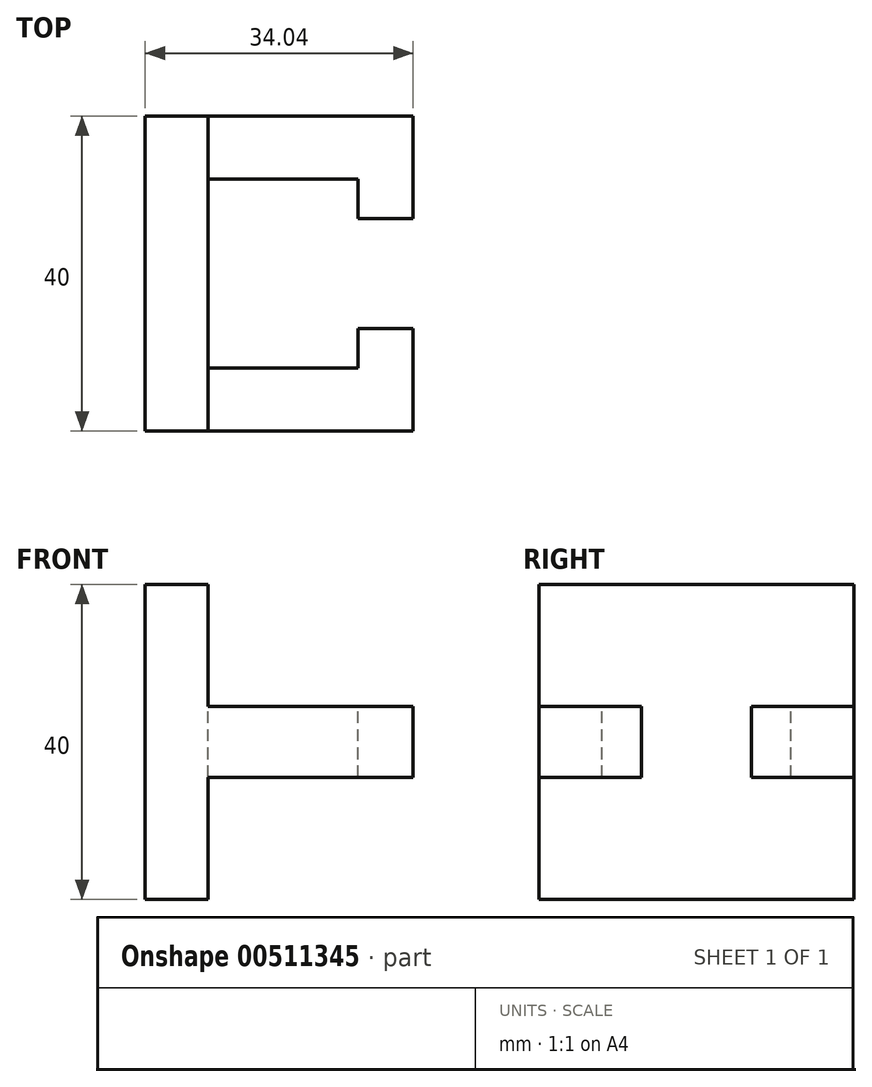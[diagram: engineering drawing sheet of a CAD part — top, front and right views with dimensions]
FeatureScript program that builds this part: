
annotation { "Feature Type Name" : "Feature", "Feature Type Description" : "" }
export const myFeature = defineFeature(function(context is Context, id is Id, definition is map)
    precondition{}
    {
        {
            var Q0;
            Q0=qCreatedBy(makeId("Top.planeOp"),FACE);
            var sketch = newSketch(context, id + "F0", { "sketchPlane" : qUnion([Q0])});
            skLineSegment(sketch, "E0.bottom", {"start": v(-20, 20) * mm, "end": v(20, 20) * mm});
            skLineSegment(sketch, "E0.top", {"start": v(-20, -20) * mm, "end": v(20, -20) * mm});
            skLineSegment(sketch, "E0.left", {"start": v(-20, 20) * mm, "end": v(-20, -20) * mm});
            skLineSegment(sketch, "E0.right", {"start": v(20, 20) * mm, "end": v(20, -20) * mm});
            skLineSegment(sketch, "E1", {"start": v(-20, 0) * mm, "end": v(20, 0) * mm, "construction": true});
            skSolve(sketch);
        }
        {
            var Q0;
            Q0=makeQuery(id+"F0.imprint","IMPRINT",FACE,{"disambiguationData":[TD([[makeQuery(id+"F0.imprint","IMPRINT",EDGE,{"derivedFrom":sQuery(id+"F0.wireOp",EDGE,"E0.bottom")}),-1.0]])]});
            extrude(context, id + "F1", {"entities" : qUnion([Q0]), "oppositeDirection" : true, "depth" : 40 * mm});
        }
        {
            var Q0;
            Q0=makeQuery(id+"F1.opExtrude","CAP_FACE",FACE,{"disambiguationData":[OSD([sQuery(id+"F0.wireOp",EDGE,"E0.bottom"),sQuery(id+"F0.wireOp",EDGE,"E0.top"),sQuery(id+"F0.wireOp",EDGE,"E0.left"),sQuery(id+"F0.wireOp",EDGE,"E0.right")])],"isStart":true});
            var sketch = newSketch(context, id + "F2", { "sketchPlane" : qUnion([Q0])});
            skLineSegment(sketch, "E2", {"start": v(-20, 20) * mm, "end": v(-20, -20) * mm});
            skLineSegment(sketch, "E3", {"start": v(-20, 20) * mm, "end": v(14.04, 20) * mm});
            skLineSegment(sketch, "E4", {"start": v(-20, -20) * mm, "end": v(14.04, -20) * mm});
            skLineSegment(sketch, "E5", {"start": v(14.04, 20) * mm, "end": v(14.04, 7) * mm});
            skLineSegment(sketch, "E6", {"start": v(14.04, -20) * mm, "end": v(14.04, -7) * mm});
            skLineSegment(sketch, "E7", {"start": v(14.04, -7) * mm, "end": v(7.04, -7) * mm});
            skLineSegment(sketch, "E8", {"start": v(7.04, -7) * mm, "end": v(7.04, -12) * mm});
            skLineSegment(sketch, "E9", {"start": v(7.04, -12) * mm, "end": v(-12, -12) * mm});
            skLineSegment(sketch, "E10", {"start": v(-12, -12) * mm, "end": v(-12, 12) * mm});
            skLineSegment(sketch, "E11", {"start": v(-12, 12) * mm, "end": v(7.04, 12) * mm});
            skLineSegment(sketch, "E12", {"start": v(7.04, 12) * mm, "end": v(7.04, 7) * mm});
            skLineSegment(sketch, "E13", {"start": v(7.04, 7) * mm, "end": v(14.04, 7) * mm});
            skSolve(sketch);
        }
        {
            var Q0;
            Q0=makeQuery(id+"F1.opExtrude","SWEPT_FACE",FACE,{"disambiguationData":[OSD([sQuery(id+"F0.wireOp",EDGE,"E0.top")])]});
            var sketch = newSketch(context, id + "F3", { "sketchPlane" : qUnion([Q0])});
            skLineSegment(sketch, "E14", {"start": v(-20, 0) * mm, "end": v(-20, -40) * mm});
            skLineSegment(sketch, "E15", {"start": v(-20, 0) * mm, "end": v(-12, 0) * mm});
            skLineSegment(sketch, "E16", {"start": v(-20, -40) * mm, "end": v(-12, -40) * mm});
            skLineSegment(sketch, "E17", {"start": v(-12, -40) * mm, "end": v(-12, -24.5) * mm});
            skLineSegment(sketch, "E18", {"start": v(-12, 0) * mm, "end": v(-12, -15.5) * mm});
            skLineSegment(sketch, "E19", {"start": v(-12, -15.5) * mm, "end": v(20, -15.5) * mm});
            skLineSegment(sketch, "E20", {"start": v(-12, -24.5) * mm, "end": v(20, -24.5) * mm});
            skSolve(sketch);
        }
        {
            var Q0;
            {var subQ2=sQuery(id+"F2.wireOp",EDGE,"E5");Q0=makeQuery(id+"F2.imprint","IMPRINT",FACE,{"disambiguationData":[TD([[makeQuery(id+"F2.imprint","IMPRINT",EDGE,{"derivedFrom":subQ2}),1.0]])]});}
            extrude(context, id + "F4", {"entities" : qUnion([Q0]), "operationType" : NewBodyOperationType.REMOVE, "oppositeDirection" : true, "depth" : 40 * mm, "offsetDistance" : 25.4 * mm});
        }
        {
            var Q0;
            {var subQ0=sQuery(id+"F3.wireOp",EDGE,"E18");Q0=makeQuery(id+"F3.imprint","IMPRINT",FACE,{"disambiguationData":[TD([[makeQuery(id+"F3.imprint","IMPRINT",EDGE,{"derivedFrom":subQ0}),1.0]])]});}
            extrude(context, id + "F5", {"entities" : qUnion([Q0]), "operationType" : NewBodyOperationType.REMOVE, "oppositeDirection" : true, "depth" : 40 * mm, "offsetDistance" : 25.4 * mm});
        }
        {
            var Q0;
            {var subQ0=sQuery(id+"F3.wireOp",EDGE,"E17");Q0=makeQuery(id+"F3.imprint","IMPRINT",FACE,{"disambiguationData":[TD([[makeQuery(id+"F3.imprint","IMPRINT",EDGE,{"derivedFrom":subQ0}),-1.0]])]});}
            extrude(context, id + "F6", {"entities" : qUnion([Q0]), "operationType" : NewBodyOperationType.REMOVE, "oppositeDirection" : true, "depth" : 40 * mm, "offsetDistance" : 25.4 * mm});
        }
    });
